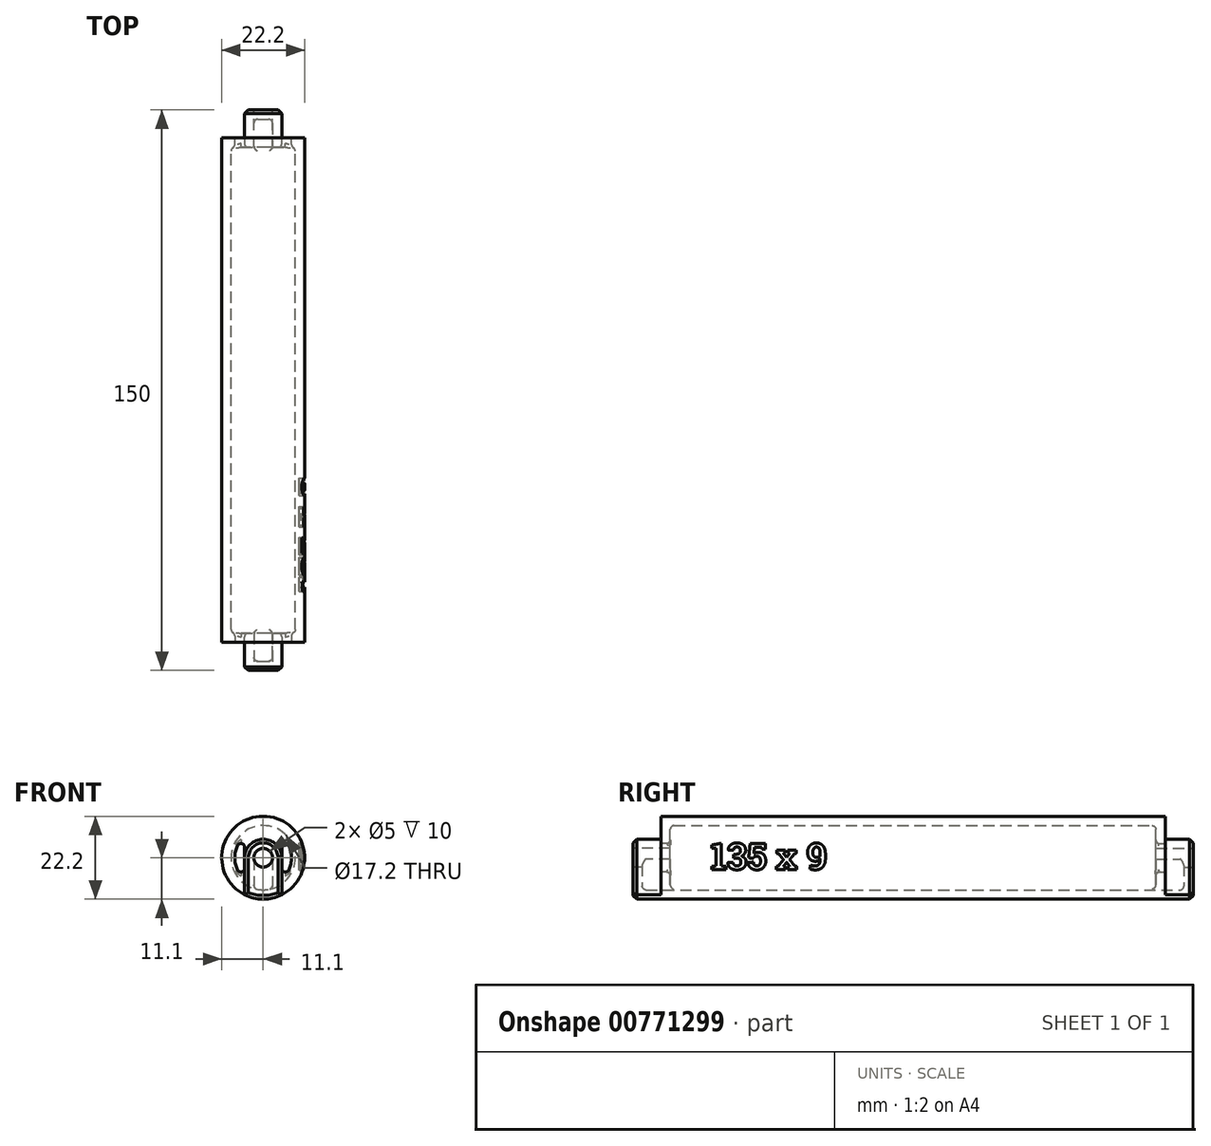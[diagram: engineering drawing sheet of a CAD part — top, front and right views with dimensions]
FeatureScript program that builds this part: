
annotation { "Feature Type Name" : "Feature", "Feature Type Description" : "" }
export const myFeature = defineFeature(function(context is Context, id is Id, definition is map)
    precondition{}
    {
        {
            var Q0;
            Q0=qCreatedBy(makeId("Front.planeOp"),FACE);
            var sketch = newSketch(context, id + "F0", { "sketchPlane" : qUnion([Q0])});
            skCircle(sketch, "E0", {"center": v(0, 0) * mm, "radius": 11.1 * mm});
            skSolve(sketch);
        }
        {
            var Q0;
            Q0 = qSketchRegion(id + "F0", true);
            extrude(context, id + "F1", {"entities" : qUnion([Q0]), "depth" : (135 / 2) * mm, "offsetDistance" : 25 * mm});
        }
        {
            var Q0;
            Q0=makeQuery(id+"F1.opExtrude","CAP_FACE",FACE,{"disambiguationData":[OSD([sQuery(id+"F0.wireOp",EDGE,"E0")])],"isStart":false});
            var sketch = newSketch(context, id + "F2", { "sketchPlane" : qUnion([Q0])});
            skArc(sketch, "E1", {"start": v(-4.97, 0) * mm, "mid": v(0, 4.97) * mm, "end": v(4.97, 0) * mm});
            skArc(sketch, "E2.0", {"start": v(-4.97, -9.92) * mm, "mid": v(0, -11.1) * mm, "end": v(4.97, -9.92) * mm});
            skLineSegment(sketch, "E3", {"start": v(-4.97, 0) * mm, "end": v(-4.97, -9.92) * mm});
            skLineSegment(sketch, "E4", {"start": v(4.97, 0) * mm, "end": v(4.97, -9.92) * mm});
            skSolve(sketch);
        }
        {
            var Q0;
            Q0 = qSketchRegion(id + "F2", true);
            extrude(context, id + "F3", {"entities" : qUnion([Q0]), "operationType" : NewBodyOperationType.ADD, "depth" : 7.5 * mm, "offsetDistance" : 25 * mm});
        }
        {
            var Q0;
            Q0=qCreatedBy(makeId("Front.planeOp"),FACE);
            var sketch = newSketch(context, id + "F4", { "sketchPlane" : qUnion([Q0])});
            skCircle(sketch, "E5.0", {"center": v(0, 0) * mm, "radius": 11.1 * mm, "construction": true});
            skLineSegment(sketch, "E6", {"start": v(0, 0) * mm, "end": v(0, 11.1) * mm, "construction": true});
            skCircle(sketch, "E7", {"center": v(0, 11.1) * mm, "radius": 3.5 * mm});
            skSolve(sketch);
        }
        {
            var Q0;
            Q0=makeQuery(id+"F1.opExtrude","CAP_FACE",FACE,{"disambiguationData":[OSD([sQuery(id+"F0.wireOp",EDGE,"E0")])],"isStart":true});
            shell(context, id + "F5", {"entities" : qUnion([Q0]), "thickness" : 2.5 * mm});
        }
        {
            var Q0;
            Q0=makeQuery(id+"F3.opExtrude","CAP_FACE",FACE,{"disambiguationData":[OSD([sQuery(id+"F2.wireOp",EDGE,"E1"),sQuery(id+"F2.wireOp",EDGE,"E2.0"),sQuery(id+"F2.wireOp",EDGE,"E3"),sQuery(id+"F2.wireOp",EDGE,"E4")])],"isStart":false});
            var sketch = newSketch(context, id + "F6", { "sketchPlane" : qUnion([Q0])});
            skPoint(sketch, "E8.0", {"position": v(0, 0) * mm});
            skSolve(sketch);
        }
        {
            var Q0;
            Q0=sQuery(id+"F6.wireOp",VERTEX,"E8.0");
            var Q1;
            Q1=makeQuery(id+"F1.opExtrude","SWEPT_BODY",BODY,{"disambiguationData":[OSD([sQuery(id+"F0.wireOp",EDGE,"E0")])]});
            hole(context, id + "F7", {"style" : HoleStyle.SIMPLE, "endStyle" : HoleEndStyle.BLIND, "holeDiameter" : 5 * mm, "majorDiameter" : 5 * mm, "holeDepth" : 12.5 * mm, "tappedDepth" : 10.1 * mm, "tapClearance" : 3, "startFromSketch" : true, "locations" : qUnion([Q0]), "scope" : qUnion([Q1])});
        }
        {
            var Q0;
            {var subQ0=sQuery(id+"F0.wireOp",EDGE,"E0");Q0=makeQuery(id+"F5.opShell","OFFSET_EDGE",EDGE,{"disambiguationData":[OSD([subQ0]),TDD([makeQuery(id+"F1.opExtrude","CAP_EDGE",EDGE,{"disambiguationData":[OSD([subQ0])],"isStart":false})])]});}
            var Q1;
            Q1=makeQuery(id+"F5.opShell","OFFSET_EDGE",EDGE,{"disambiguationData":[OSD([sQuery(id+"F0.wireOp",EDGE,"E0"),sQuery(id+"F2.wireOp",EDGE,"E2.0"),sQuery(id+"F2.wireOp",EDGE,"E4")])]});
            var Q2;
            Q2=makeQuery(id+"F5.opShell","OFFSET_EDGE",EDGE,{"disambiguationData":[OSD([sQuery(id+"F2.wireOp",EDGE,"E2.0")])]});
            var Q3;
            Q3=makeQuery(id+"F5.opShell","OFFSET_EDGE",EDGE,{"disambiguationData":[OSD([sQuery(id+"F0.wireOp",EDGE,"E0"),sQuery(id+"F2.wireOp",EDGE,"E2.0"),sQuery(id+"F2.wireOp",EDGE,"E3")])]});
            var Q4;
            {var subQ0=sQuery(id+"F2.wireOp",EDGE,"E3");Q4=makeQuery(id+"F5.opShell","OFFSET_EDGE",EDGE,{"disambiguationData":[OSD([subQ0]),TDD([makeQuery(id+"F3.opExtrude","CAP_EDGE",EDGE,{"disambiguationData":[OSD([subQ0])],"isStart":false})])]});}
            var Q5;
            {var subQ0=sQuery(id+"F2.wireOp",EDGE,"E4");Q5=makeQuery(id+"F5.opShell","OFFSET_EDGE",EDGE,{"disambiguationData":[OSD([subQ0]),TDD([makeQuery(id+"F3.opExtrude","CAP_EDGE",EDGE,{"disambiguationData":[OSD([subQ0])],"isStart":false})])]});}
            var Q6;
            {var subQ0=sQuery(id+"F2.wireOp",EDGE,"E3");Q6=makeQuery(id+"F5.opShell","OFFSET_EDGE",EDGE,{"disambiguationData":[OSD([subQ0]),TDD([makeQuery(id+"F3.opExtrude","CAP_EDGE",EDGE,{"disambiguationData":[OSD([subQ0])],"isStart":true})])]});}
            var Q7;
            Q7=makeQuery(id+"F7.hole-0.boolean.opBoolean","INTERSECT",EDGE,{"derivedFrom":[makeQuery(id+"F5.opShell","OFFSET_FACE",FACE,{"disambiguationData":[OSD([sQuery(id+"F0.wireOp",EDGE,"E0")])]}),makeQuery(id+"F7.hole-0.opRevolve","SWEPT_FACE",FACE,{"disambiguationData":[OSD([sQuery(id+"F7.hole-0.sketch.wireOp",EDGE,"core_line_2")])]})]});
            var Q8;
            Q8=makeQuery(id+"F7.hole-0.boolean.opBoolean","INTERSECT",EDGE,{"derivedFrom":[makeQuery(id+"F5.opShell","OFFSET_FACE",FACE,{"disambiguationData":[OSD([sQuery(id+"F2.wireOp",EDGE,"E1"),sQuery(id+"F2.wireOp",EDGE,"E2.0"),sQuery(id+"F2.wireOp",EDGE,"E3"),sQuery(id+"F2.wireOp",EDGE,"E4")])]}),makeQuery(id+"F7.hole-0.opRevolve","SWEPT_FACE",FACE,{"disambiguationData":[OSD([sQuery(id+"F7.hole-0.sketch.wireOp",EDGE,"core_line_2")])]})]});
            fillet(context, id + "F8", {"entities" : qUnion([Q0, Q1, Q2, Q3, Q4, Q5, Q6, Q7, Q8]), "radius" : 1 * mm, "tangentPropagation" : true, "allowEdgeOverflow" : false});
        }
        {
            var Q0;
            Q0=makeQuery(id+"F1.opExtrude","CAP_FACE",FACE,{"disambiguationData":[OSD([sQuery(id+"F0.wireOp",EDGE,"E0")])],"isStart":false});
            var sketch = newSketch(context, id + "F9", { "sketchPlane" : qUnion([Q0])});
            skLineSegment(sketch, "E9.1", {"start": v(-4.97, 0) * mm, "end": v(-4.97, -5.75) * mm});
            skArc(sketch, "E9.2", {"start": v(-4.97, -5.75) * mm, "mid": v(-7.6, 0) * mm, "end": v(-4.98, 5.75) * mm});
            skLineSegment(sketch, "E9.3", {"start": v(4.97, 0) * mm, "end": v(4.97, -5.75) * mm});
            skLineSegment(sketch, "E10", {"start": v(-4.97, 0) * mm, "end": v(-4.97, 5.75) * mm});
            skLineSegment(sketch, "E11", {"start": v(4.97, 0) * mm, "end": v(4.97, 5.75) * mm});
            skArc(sketch, "E12.trimOffspring", {"start": v(4.97, 5.75) * mm, "mid": v(7.6, 0) * mm, "end": v(4.97, -5.75) * mm});
            skPoint(sketch, "E13.orphan", {"position": v(-4.97, -9.92) * mm});
            skPoint(sketch, "E14.orphan", {"position": v(4.97, -9.92) * mm});
            skPoint(sketch, "E15.orphan", {"position": v(2.47, -7.19) * mm});
            skPoint(sketch, "E16.orphan", {"position": v(-2.47, -7.19) * mm});
            skSolve(sketch);
        }
        {
            var Q0;
            Q0 = qSketchRegion(id + "F9", true);
            extrude(context, id + "F10", {"entities" : qUnion([Q0]), "operationType" : NewBodyOperationType.REMOVE, "oppositeDirection" : true, "depth" : 25 * mm, "offsetDistance" : 25 * mm});
        }
        {
            var Q0;
            Q0=makeQuery(id+"F10.boolean.opBoolean","COPY",EDGE,{"derivedFrom":makeQuery(id+"F10.opExtrude","SWEPT_EDGE",EDGE,{"disambiguationData":[OSD([sQuery(id+"F2.wireOp",EDGE,"E4"),sQuery(id+"F9.wireOp",EDGE,"E9.3"),sQuery(id+"F9.wireOp",EDGE,"E12.trimOffspring")])]})});
            var Q1;
            Q1=makeQuery(id+"F10.boolean.opBoolean","COPY",EDGE,{"derivedFrom":makeQuery(id+"F10.opExtrude","SWEPT_EDGE",EDGE,{"disambiguationData":[OSD([sQuery(id+"F2.wireOp",EDGE,"E3"),sQuery(id+"F9.wireOp",EDGE,"E9.1"),sQuery(id+"F9.wireOp",EDGE,"E9.2")])]})});
            var Q2;
            Q2=makeQuery(id+"F10.boolean.opBoolean","COPY",EDGE,{"derivedFrom":makeQuery(id+"F10.opExtrude","SWEPT_EDGE",EDGE,{"disambiguationData":[OSD([sQuery(id+"F9.wireOp",EDGE,"E9.2"),sQuery(id+"F9.wireOp",EDGE,"E10")])]})});
            var Q3;
            Q3=makeQuery(id+"F10.boolean.opBoolean","COPY",EDGE,{"derivedFrom":makeQuery(id+"F10.opExtrude","SWEPT_EDGE",EDGE,{"disambiguationData":[OSD([sQuery(id+"F9.wireOp",EDGE,"E11"),sQuery(id+"F9.wireOp",EDGE,"E12.trimOffspring")])]})});
            fillet(context, id + "F11", {"entities" : qUnion([Q0, Q1, Q2, Q3]), "radius" : 1 * mm, "tangentPropagation" : true, "allowEdgeOverflow" : false});
        }
        {
            var Q0;
            Q0=makeQuery(id+"F3.opExtrude","CAP_EDGE",EDGE,{"disambiguationData":[OSD([sQuery(id+"F2.wireOp",EDGE,"E1")])],"isStart":false});
            var Q1;
            Q1=makeQuery(id+"F3.opExtrude","CAP_EDGE",EDGE,{"disambiguationData":[OSD([sQuery(id+"F2.wireOp",EDGE,"E3")])],"isStart":false});
            var Q2;
            Q2=makeQuery(id+"F3.opExtrude","CAP_EDGE",EDGE,{"disambiguationData":[OSD([sQuery(id+"F2.wireOp",EDGE,"E2.0")])],"isStart":false});
            chamfer(context, id + "F12", {"entities" : qUnion([Q0, Q1, Q2]), "width" : 1 * mm, "tangentPropagation" : true});
        }
        {
            var Q0;
            Q0=makeQuery(id+"F1.opExtrude","SWEPT_BODY",BODY,{"disambiguationData":[OSD([sQuery(id+"F0.wireOp",EDGE,"E0")])]});
            var Q1;
            Q1=makeQuery(id+"F1.opExtrude","CAP_FACE",FACE,{"disambiguationData":[OSD([sQuery(id+"F0.wireOp",EDGE,"E0")])],"isStart":true});
            mirror(context, id + "F13", {"operationType" : NewBodyOperationType.ADD, "entities" : qUnion([Q0]), "mirrorPlane" : qUnion([Q1])});
        }
        {
            var Q0;
            Q0=qCreatedBy(makeId("Right.planeOp"),FACE);
            cPlane(context, id + "F14", {"entities" : qUnion([Q0]), "cplaneType" : CPlaneType.OFFSET, "offset" : 11.1 * mm, "width" : 150 * mm, "height" : 150 * mm});
        }
        {
            var Q0;
            Q0=qCreatedBy(id+"F14.planeOp",FACE);
            var sketch = newSketch(context, id + "F15", { "sketchPlane" : qUnion([Q0])});
            skText(sketch, "E17", { "text": "135 x 9\n", "fontName": "RobotoSlab-Bold.ttf"});
            const initialGuessF15  = {"E17": [-0.0542, -0.00317, 1, 0, 0.00713]};
            skSetInitialGuess(sketch, initialGuessF15);
            skSolve(sketch);
        }
        {
            var Q0;
            Q0 = qSketchRegion(id + "F15", true);
            extrude(context, id + "F16", {"entities" : qUnion([Q0]), "operationType" : NewBodyOperationType.REMOVE, "oppositeDirection" : true, "depth" : 1.5 * mm, "offsetDistance" : 25 * mm});
        }
        {
            var Q0;
            Q0=makeQuery(id+"F11.opFillet","BLEND_EDGE",EDGE,{"blendedFrom":[makeQuery(id+"F10.boolean.opBoolean","COPY",EDGE,{"derivedFrom":makeQuery(id+"F10.opExtrude","SWEPT_EDGE",EDGE,{"disambiguationData":[OSD([sQuery(id+"F9.wireOp",EDGE,"E9.2"),sQuery(id+"F9.wireOp",EDGE,"E10")])]})}),makeQuery(id+"F5.opShell","OFFSET_FACE",FACE,{"disambiguationData":[OSD([sQuery(id+"F0.wireOp",EDGE,"E0")])]})],"blendedInto":[makeQuery(id+"F5.opShell","OFFSET_FACE",FACE,{"disambiguationData":[OSD([sQuery(id+"F0.wireOp",EDGE,"E0")])]})]});
            var Q1;
            Q1=makeQuery(id+"F10.boolean.opBoolean","INTERSECT",EDGE,{"derivedFrom":[makeQuery(id+"F5.opShell","OFFSET_FACE",FACE,{"disambiguationData":[OSD([sQuery(id+"F0.wireOp",EDGE,"E0")])]}),makeQuery(id+"F10.opExtrude","SWEPT_FACE",FACE,{"disambiguationData":[OSD([sQuery(id+"F9.wireOp",EDGE,"E9.1"),sQuery(id+"F9.wireOp",EDGE,"E10")])]})]});
            var Q2;
            Q2=makeQuery(id+"F11.opFillet","BLEND_EDGE",EDGE,{"blendedFrom":[makeQuery(id+"F10.boolean.opBoolean","COPY",EDGE,{"derivedFrom":makeQuery(id+"F10.opExtrude","SWEPT_EDGE",EDGE,{"disambiguationData":[OSD([sQuery(id+"F2.wireOp",EDGE,"E3"),sQuery(id+"F9.wireOp",EDGE,"E9.1"),sQuery(id+"F9.wireOp",EDGE,"E9.2")])]})}),makeQuery(id+"F5.opShell","OFFSET_FACE",FACE,{"disambiguationData":[OSD([sQuery(id+"F0.wireOp",EDGE,"E0")])]})],"blendedInto":[makeQuery(id+"F5.opShell","OFFSET_FACE",FACE,{"disambiguationData":[OSD([sQuery(id+"F0.wireOp",EDGE,"E0")])]})]});
            var Q3;
            Q3=makeQuery(id+"F13.opPattern","COPY",EDGE,{"derivedFrom":makeQuery(id+"F10.boolean.opBoolean","INTERSECT",EDGE,{"derivedFrom":[makeQuery(id+"F5.opShell","OFFSET_FACE",FACE,{"disambiguationData":[OSD([sQuery(id+"F0.wireOp",EDGE,"E0")])]}),makeQuery(id+"F10.opExtrude","SWEPT_FACE",FACE,{"disambiguationData":[OSD([sQuery(id+"F9.wireOp",EDGE,"E9.1"),sQuery(id+"F9.wireOp",EDGE,"E10")])]})]}),"instanceName":"1"});
            var Q4;
            Q4=makeQuery(id+"F13.opPattern","COPY",EDGE,{"derivedFrom":makeQuery(id+"F11.opFillet","BLEND_EDGE",EDGE,{"blendedFrom":[makeQuery(id+"F10.boolean.opBoolean","COPY",EDGE,{"derivedFrom":makeQuery(id+"F10.opExtrude","SWEPT_EDGE",EDGE,{"disambiguationData":[OSD([sQuery(id+"F9.wireOp",EDGE,"E9.2"),sQuery(id+"F9.wireOp",EDGE,"E10")])]})}),makeQuery(id+"F5.opShell","OFFSET_FACE",FACE,{"disambiguationData":[OSD([sQuery(id+"F0.wireOp",EDGE,"E0")])]})],"blendedInto":[makeQuery(id+"F5.opShell","OFFSET_FACE",FACE,{"disambiguationData":[OSD([sQuery(id+"F0.wireOp",EDGE,"E0")])]})]}),"instanceName":"1"});
            fillet(context, id + "F17", {"entities" : qUnion([Q0, Q1, Q2, Q3, Q4]), "radius" : 1 * mm, "tangentPropagation" : true, "allowEdgeOverflow" : false});
        }
        {
            var Q0;
            Q0=makeQuery(id+"F10.boolean.opBoolean","INTERSECT",EDGE,{"derivedFrom":[makeQuery(id+"F5.opShell","OFFSET_FACE",FACE,{"disambiguationData":[OSD([sQuery(id+"F0.wireOp",EDGE,"E0")])]}),makeQuery(id+"F10.opExtrude","SWEPT_FACE",FACE,{"disambiguationData":[OSD([sQuery(id+"F9.wireOp",EDGE,"E9.3"),sQuery(id+"F9.wireOp",EDGE,"E11")])]})]});
            var Q1;
            Q1=makeQuery(id+"F11.opFillet","BLEND_EDGE",EDGE,{"blendedFrom":[makeQuery(id+"F10.boolean.opBoolean","COPY",EDGE,{"derivedFrom":makeQuery(id+"F10.opExtrude","SWEPT_EDGE",EDGE,{"disambiguationData":[OSD([sQuery(id+"F9.wireOp",EDGE,"E11"),sQuery(id+"F9.wireOp",EDGE,"E12.trimOffspring")])]})}),makeQuery(id+"F5.opShell","OFFSET_FACE",FACE,{"disambiguationData":[OSD([sQuery(id+"F0.wireOp",EDGE,"E0")])]})],"blendedInto":[makeQuery(id+"F5.opShell","OFFSET_FACE",FACE,{"disambiguationData":[OSD([sQuery(id+"F0.wireOp",EDGE,"E0")])]})]});
            var Q2;
            Q2=makeQuery(id+"F11.opFillet","BLEND_EDGE",EDGE,{"blendedFrom":[makeQuery(id+"F10.boolean.opBoolean","COPY",EDGE,{"derivedFrom":makeQuery(id+"F10.opExtrude","SWEPT_EDGE",EDGE,{"disambiguationData":[OSD([sQuery(id+"F2.wireOp",EDGE,"E4"),sQuery(id+"F9.wireOp",EDGE,"E9.3"),sQuery(id+"F9.wireOp",EDGE,"E12.trimOffspring")])]})}),makeQuery(id+"F5.opShell","OFFSET_FACE",FACE,{"disambiguationData":[OSD([sQuery(id+"F0.wireOp",EDGE,"E0")])]})],"blendedInto":[makeQuery(id+"F5.opShell","OFFSET_FACE",FACE,{"disambiguationData":[OSD([sQuery(id+"F0.wireOp",EDGE,"E0")])]})]});
            var Q3;
            Q3=makeQuery(id+"F13.opPattern","COPY",EDGE,{"derivedFrom":makeQuery(id+"F11.opFillet","BLEND_EDGE",EDGE,{"blendedFrom":[makeQuery(id+"F10.boolean.opBoolean","COPY",EDGE,{"derivedFrom":makeQuery(id+"F10.opExtrude","SWEPT_EDGE",EDGE,{"disambiguationData":[OSD([sQuery(id+"F9.wireOp",EDGE,"E11"),sQuery(id+"F9.wireOp",EDGE,"E12.trimOffspring")])]})}),makeQuery(id+"F5.opShell","OFFSET_FACE",FACE,{"disambiguationData":[OSD([sQuery(id+"F0.wireOp",EDGE,"E0")])]})],"blendedInto":[makeQuery(id+"F5.opShell","OFFSET_FACE",FACE,{"disambiguationData":[OSD([sQuery(id+"F0.wireOp",EDGE,"E0")])]})]}),"instanceName":"1"});
            var Q4;
            Q4=makeQuery(id+"F13.opPattern","COPY",EDGE,{"derivedFrom":makeQuery(id+"F10.boolean.opBoolean","INTERSECT",EDGE,{"derivedFrom":[makeQuery(id+"F5.opShell","OFFSET_FACE",FACE,{"disambiguationData":[OSD([sQuery(id+"F0.wireOp",EDGE,"E0")])]}),makeQuery(id+"F10.opExtrude","SWEPT_FACE",FACE,{"disambiguationData":[OSD([sQuery(id+"F9.wireOp",EDGE,"E9.3"),sQuery(id+"F9.wireOp",EDGE,"E11")])]})]}),"instanceName":"1"});
            fillet(context, id + "F18", {"entities" : qUnion([Q0, Q1, Q2, Q3, Q4]), "radius" : 1 * mm, "tangentPropagation" : true, "allowEdgeOverflow" : false});
        }
    });
